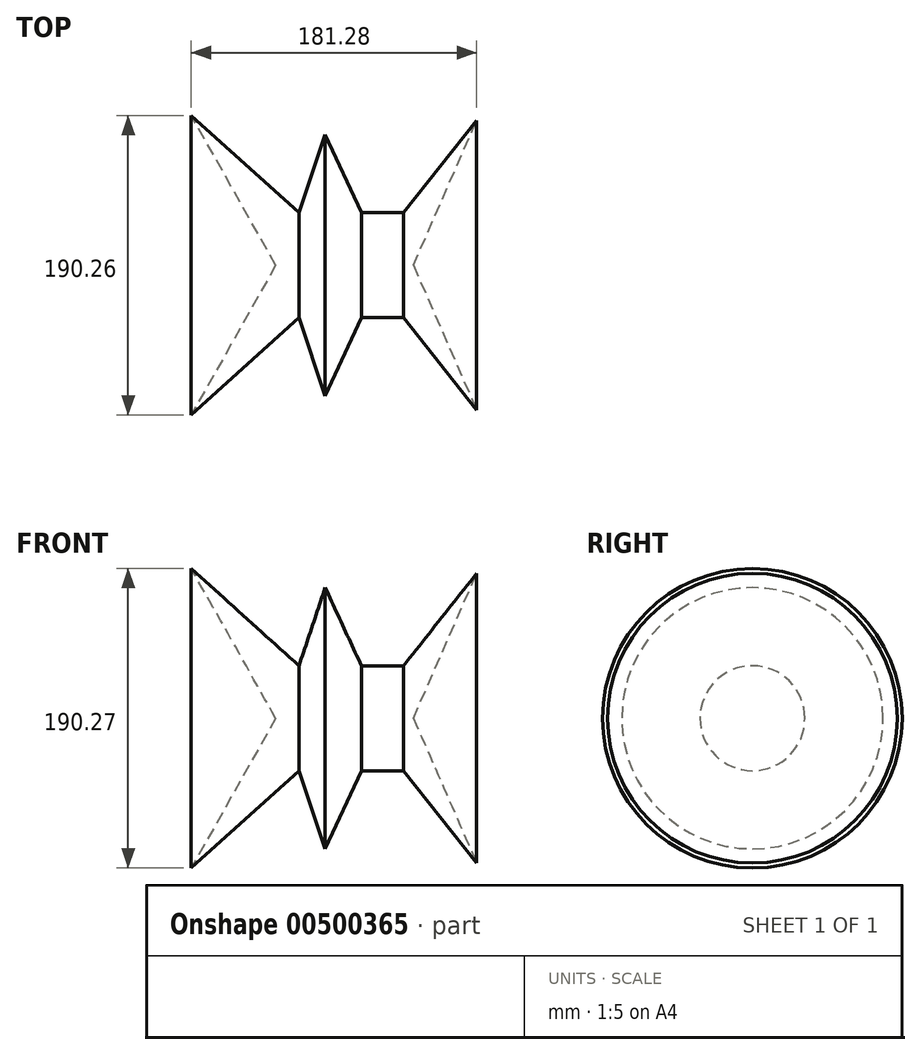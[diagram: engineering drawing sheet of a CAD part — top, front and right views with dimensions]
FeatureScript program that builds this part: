
annotation { "Feature Type Name" : "Feature", "Feature Type Description" : "" }
export const myFeature = defineFeature(function(context is Context, id is Id, definition is map)
    precondition{}
    {
        {
            var Q0;
            Q0=qCreatedBy(makeId("Front.planeOp"),FACE);
            var sketch = newSketch(context, id + "F0", { "sketchPlane" : qUnion([Q0])});
            skLineSegment(sketch, "E0", {"start": v(-31.45, 65.54) * mm, "end": v(-85.1, -29.6) * mm});
            skLineSegment(sketch, "E1", {"start": v(-31.45, 65.54) * mm, "end": v(56.02, 65.54) * mm});
            skLineSegment(sketch, "E2", {"start": v(56.02, 65.54) * mm, "end": v(96.2, -26.43) * mm});
            skLineSegment(sketch, "E3", {"start": v(-85.1, -29.6) * mm, "end": v(-16.65, 32.24) * mm});
            skLineSegment(sketch, "E4", {"start": v(-16.65, 32.24) * mm, "end": v(0, -17.44) * mm});
            skLineSegment(sketch, "E5", {"start": v(0, -17.44) * mm, "end": v(23, 32.24) * mm});
            skLineSegment(sketch, "E6", {"start": v(23, 32.24) * mm, "end": v(49.68, 32.24) * mm});
            skLineSegment(sketch, "E7", {"start": v(49.42, 32.5) * mm, "end": v(96.2, -26.43) * mm});
            skSolve(sketch);
        }
        {
            var Q0;
            Q0=makeQuery(id+"F0.imprint","IMPRINT",FACE,{"disambiguationData":[TD([[makeQuery(id+"F0.imprint","IMPRINT",EDGE,{"derivedFrom":sQuery(id+"F0.wireOp",EDGE,"E0")}),1.0]])]});
            var Q1;
            Q1=sQuery(id+"F0.wireOp",EDGE,"E1");
            revolve(context, id + "F1", {"entities" : qUnion([Q0]), "axis" : qUnion([Q1]), "revolveType" : RevolveType.FULL});
        }
    });
